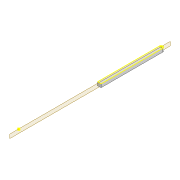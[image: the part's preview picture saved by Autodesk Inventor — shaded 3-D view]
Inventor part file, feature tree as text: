
AUTODESK INVENTOR PART (.ipt)
format: ipt  version: 2022 (Build 260153000, 153)  size: 126,464 bytes
history: native  units: mm
features: sketch x4, extrude x2, projected_geometry x2
ambient origin geometry x8: Origin, YZ Plane, XZ Plane, XY Plane, X Axis, Y Axis, Z Axis, Center Point
bodies: Solid1 (feature_tree)
feature tree (8):
  extrude  "Extrusion1"  Depth=8.0mm
  sketch  "Sketch2"  dims[d2=3.0mm d3=3.0mm]
  extrude  "Extrusion2"  Depth=3.0mm
  sketch  "Sketch4"  dims[d12=3.0mm d13=50.8mm d14=100.0mm d15=40.0mm d16=200.0mm d17=200.0mm d18=20.0mm d19=0.0mm d20=0.5mm d21=0.872665mm]
  sketch  "Sketch1"  dims[d0=319.927mm d1=8.0mm]
  projected_geometry  "Projected Loop1"
  sketch  "Sketch3"  dims[d4=8.0mm d5=0.0mm]
  projected_geometry  "Projected Loop2"
